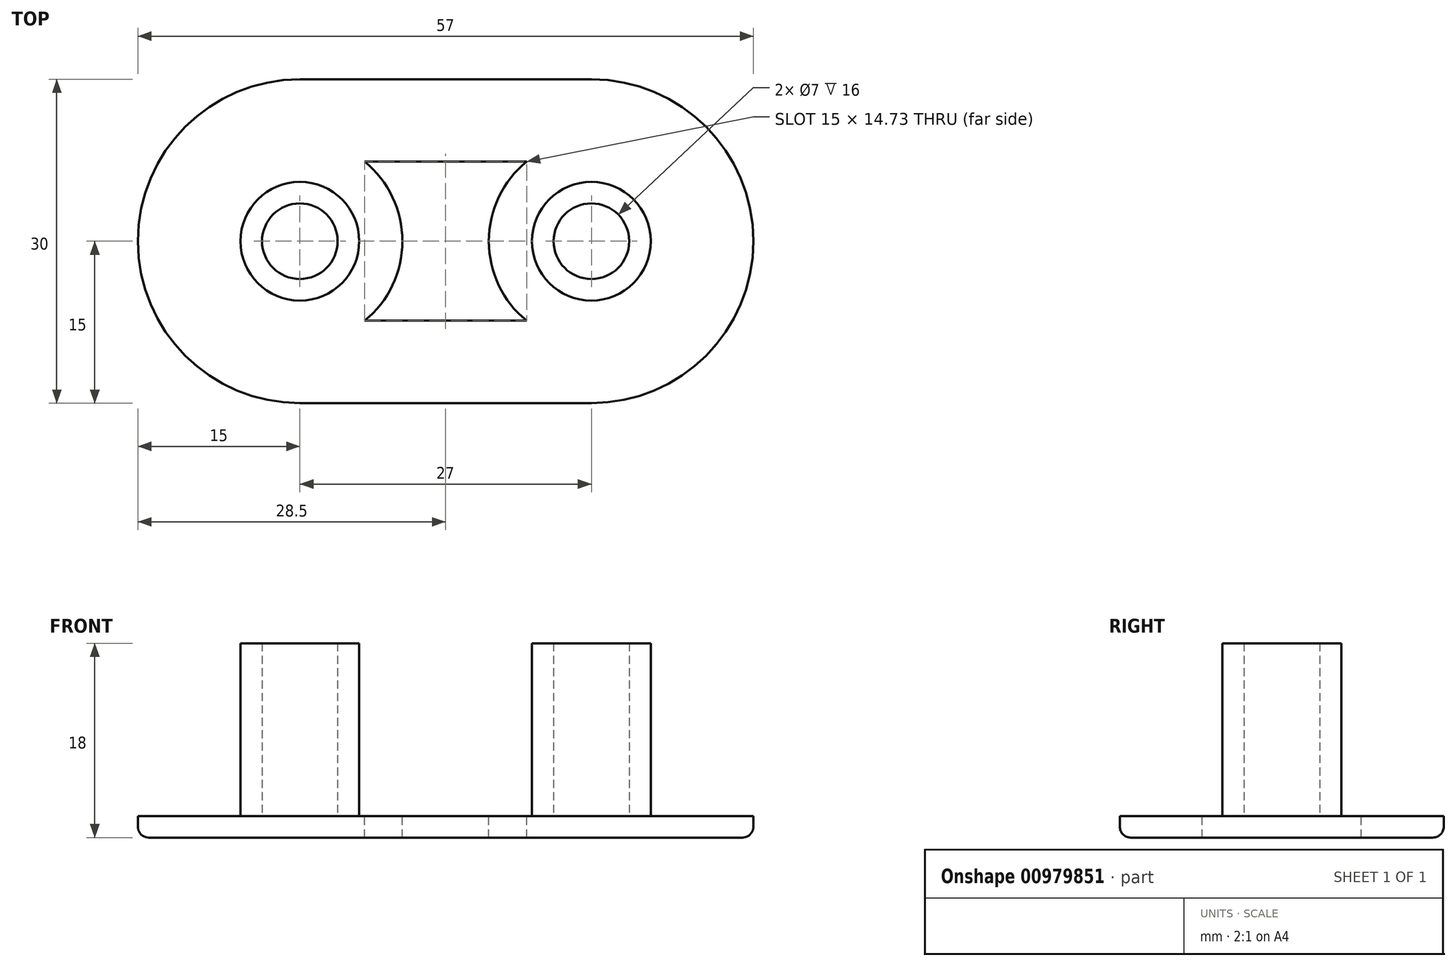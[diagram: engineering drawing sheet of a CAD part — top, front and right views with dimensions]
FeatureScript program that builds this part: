
annotation { "Feature Type Name" : "Feature", "Feature Type Description" : "" }
export const myFeature = defineFeature(function(context is Context, id is Id, definition is map)
    precondition{}
    {
        {
            var Q0;
            Q0=qCreatedBy(makeId("Top.planeOp"),FACE);
            var sketch = newSketch(context, id + "F0", { "sketchPlane" : qUnion([Q0])});
            skCircle(sketch, "E0", {"center": v(-15, 0) * mm, "radius": 15 * mm});
            skCircle(sketch, "E1", {"center": v(12, 0) * mm, "radius": 15 * mm});
            skLineSegment(sketch, "E2", {"start": v(-15, 0) * mm, "end": v(12, 0) * mm, "construction": true});
            skLineSegment(sketch, "E3", {"start": v(-15, -15) * mm, "end": v(12, -15) * mm});
            skLineSegment(sketch, "E4", {"start": v(-15, 15) * mm, "end": v(12, 15) * mm});
            skSolve(sketch);
        }
        {
            var Q0;
            {var subQ0=sQuery(id+"F0.wireOp",EDGE,"E0");var subQ1=makeQuery(id+"F0.imprint","INTERSECT",VERTEX,{"derivedFrom":[subQ0,sQuery(id+"F0.wireOp",EDGE,"E4")]});Q0=makeQuery(id+"F0.imprint","IMPRINT",FACE,{"disambiguationData":[TD([[makeQuery(id+"F0.imprint","IMPRINT",EDGE,{"disambiguationData":[TD([[subQ1,1.0]])],"derivedFrom":subQ0}),1.0]])]});}
            var Q1;
            {var subQ0=sQuery(id+"F0.wireOp",EDGE,"E4");Q1=makeQuery(id+"F0.imprint","IMPRINT",FACE,{"disambiguationData":[TD([[makeQuery(id+"F0.imprint","IMPRINT",EDGE,{"derivedFrom":subQ0}),-1.0]])]});}
            var Q2;
            {var subQ0=sQuery(id+"F0.wireOp",EDGE,"E1");var subQ1=sQuery(id+"F0.wireOp",EDGE,"E0");var subQ2=makeQuery(id+"F0.imprint","INTERSECT",VERTEX,{"disambiguationData":[OD(0.0)],"derivedFrom":[subQ1,subQ0]});Q2=makeQuery(id+"F0.imprint","IMPRINT",FACE,{"disambiguationData":[TD([[makeQuery(id+"F0.imprint","IMPRINT",EDGE,{"disambiguationData":[TD([[subQ2,1.0]])],"derivedFrom":subQ1}),-1.0]])]});}
            var Q3;
            {var subQ0=sQuery(id+"F0.wireOp",EDGE,"E1");var subQ1=sQuery(id+"F0.wireOp",EDGE,"E0");var subQ2=makeQuery(id+"F0.imprint","INTERSECT",VERTEX,{"disambiguationData":[OD(0.0)],"derivedFrom":[subQ1,subQ0]});Q3=makeQuery(id+"F0.imprint","IMPRINT",FACE,{"disambiguationData":[TD([[makeQuery(id+"F0.imprint","IMPRINT",EDGE,{"disambiguationData":[TD([[subQ2,1.0]])],"derivedFrom":subQ1}),1.0]])]});}
            var Q4;
            {var subQ0=sQuery(id+"F0.wireOp",EDGE,"E3");Q4=makeQuery(id+"F0.imprint","IMPRINT",FACE,{"disambiguationData":[TD([[makeQuery(id+"F0.imprint","IMPRINT",EDGE,{"derivedFrom":subQ0}),1.0]])]});}
            var Q5;
            {var subQ0=sQuery(id+"F0.wireOp",EDGE,"E1");var subQ1=makeQuery(id+"F0.imprint","INTERSECT",VERTEX,{"derivedFrom":[subQ0,sQuery(id+"F0.wireOp",EDGE,"E4")]});Q5=makeQuery(id+"F0.imprint","IMPRINT",FACE,{"disambiguationData":[TD([[makeQuery(id+"F0.imprint","IMPRINT",EDGE,{"disambiguationData":[TD([[subQ1,-1.0]])],"derivedFrom":subQ0}),1.0]])]});}
            extrude(context, id + "F1", {"entities" : qUnion([Q0, Q1, Q2, Q3, Q4, Q5]), "depth" : 2 * mm, "offsetDistance" : 25 * mm});
        }
        {
            var Q0;
            Q0=makeQuery(id+"F1.opExtrude","CAP_FACE",FACE,{"disambiguationData":[OSD([sQuery(id+"F0.wireOp",EDGE,"E0"),sQuery(id+"F0.wireOp",EDGE,"E1"),sQuery(id+"F0.wireOp",EDGE,"E3"),sQuery(id+"F0.wireOp",EDGE,"E4")])],"isStart":false});
            var sketch = newSketch(context, id + "F2", { "sketchPlane" : qUnion([Q0])});
            skArc(sketch, "E5.0", {"start": v(12, -15) * mm, "mid": v(27, 0) * mm, "end": v(12, 15) * mm, "construction": true});
            skArc(sketch, "E6.0", {"start": v(-15, 15) * mm, "mid": v(-30, 0) * mm, "end": v(-15, -15) * mm, "construction": true});
            skCircle(sketch, "E7", {"center": v(-15, 0) * mm, "radius": 5.5 * mm});
            skCircle(sketch, "E8", {"center": v(12, 0) * mm, "radius": 5.5 * mm});
            skCircle(sketch, "E9.0", {"center": v(-15, 0) * mm, "radius": 3.5 * mm});
            skCircle(sketch, "E10.0", {"center": v(12, 0) * mm, "radius": 3.5 * mm});
            skSolve(sketch);
        }
        {
            var Q0;
            Q0 = qSketchRegion(id + "F2", true);
            extrude(context, id + "F3", {"entities" : qUnion([Q0]), "operationType" : NewBodyOperationType.ADD, "depth" : 16 * mm, "offsetDistance" : 25 * mm});
        }
        {
            var Q0;
            {var subQ0=sQuery(id+"F0.wireOp",EDGE,"E3");var subQ1=sQuery(id+"F0.wireOp",EDGE,"E1");var subQ2=sQuery(id+"F0.wireOp",EDGE,"E4");var subQ3=sQuery(id+"F0.wireOp",EDGE,"E0");Q0=makeQuery(id+"F3.boolean.opBoolean","SPLIT",FACE,{"disambiguationData":[TD([makeQuery(id+"F1.opExtrude","SWEPT_FACE",FACE,{"disambiguationData":[OSD([subQ3])]})])],"derivedFrom":makeQuery(id+"F1.opExtrude","CAP_FACE",FACE,{"disambiguationData":[OSD([subQ3,subQ1,subQ0,subQ2])],"isStart":false})});}
            var sketch = newSketch(context, id + "F4", { "sketchPlane" : qUnion([Q0])});
            skCircle(sketch, "E11.0", {"center": v(-15, 0) * mm, "radius": 9.5 * mm});
            skCircle(sketch, "E12.0", {"center": v(12, 0) * mm, "radius": 9.5 * mm});
            skLineSegment(sketch, "E13", {"start": v(-9, -7.37) * mm, "end": v(6, -7.37) * mm});
            skLineSegment(sketch, "E14", {"start": v(6, -7.37) * mm, "end": v(6, 7.37) * mm});
            skLineSegment(sketch, "E15", {"start": v(6, 7.37) * mm, "end": v(-9, 7.37) * mm});
            skSolve(sketch);
        }
        {
            var Q0;
            {var subQ0=sQuery(id+"F4.wireOp",EDGE,"E13");Q0=makeQuery(id+"F4.imprint","IMPRINT",FACE,{"disambiguationData":[TD([[makeQuery(id+"F4.imprint","IMPRINT",EDGE,{"derivedFrom":subQ0}),1.0]])]});}
            extrude(context, id + "F5", {"entities" : qUnion([Q0]), "operationType" : NewBodyOperationType.REMOVE, "endBound" : BoundingType.UP_TO_NEXT, "oppositeDirection" : true, "depth" : 25 * mm, "offsetDistance" : 25 * mm});
        }
        {
            var Q0;
            Q0=makeQuery(id+"F5.boolean.opBoolean","COPY",EDGE,{"derivedFrom":makeQuery(id+"F5.opExtrude","CAP_EDGE",EDGE,{"disambiguationData":[OSD([sQuery(id+"F4.wireOp",EDGE,"E12.0")])],"isStart":false})});
            var Q1;
            Q1=makeQuery(id+"F5.boolean.opBoolean","COPY",EDGE,{"derivedFrom":makeQuery(id+"F5.opExtrude","CAP_EDGE",EDGE,{"disambiguationData":[OSD([sQuery(id+"F4.wireOp",EDGE,"E11.0")])],"isStart":false})});
            var Q2;
            Q2=makeQuery(id+"F1.opExtrude","CAP_EDGE",EDGE,{"disambiguationData":[OSD([sQuery(id+"F0.wireOp",EDGE,"E0")])],"isStart":true});
            var Q3;
            Q3=makeQuery(id+"F1.opExtrude","CAP_EDGE",EDGE,{"disambiguationData":[OSD([sQuery(id+"F0.wireOp",EDGE,"E3")])],"isStart":true});
            fillet(context, id + "F6", {"entities" : qUnion([Q0, Q1, Q2, Q3]), "radius" : 1 * mm, "tangentPropagation" : true, "allowEdgeOverflow" : false});
        }
    });
